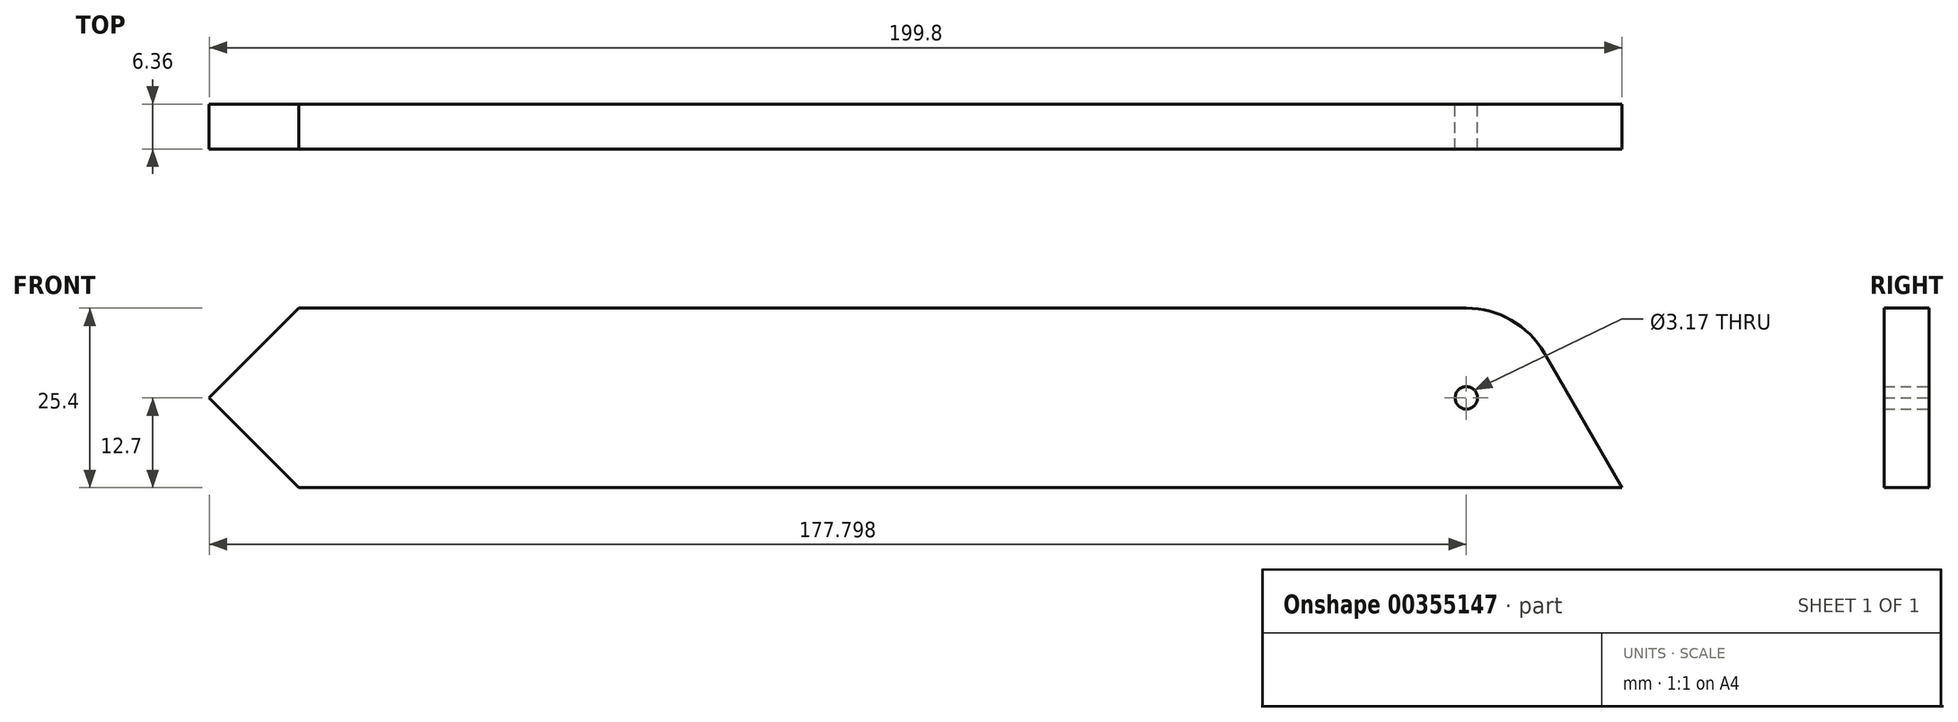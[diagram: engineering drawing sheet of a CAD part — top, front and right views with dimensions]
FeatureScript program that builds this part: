
annotation { "Feature Type Name" : "Feature", "Feature Type Description" : "" }
export const myFeature = defineFeature(function(context is Context, id is Id, definition is map)
    precondition{}
    {
        {
            var Q0;
            Q0=qCreatedBy(makeId("Front.planeOp"),FACE);
            var sketch = newSketch(context, id + "F0", { "sketchPlane" : qUnion([Q0])});
            skLineSegment(sketch, "E0", {"start": v(87.99, -152.4) * mm, "end": v(-263.96, -152.4) * mm});
            skLineSegment(sketch, "E1", {"start": v(-263.96, -152.4) * mm, "end": v(0, 0) * mm});
            skLineSegment(sketch, "E2", {"start": v(0, 0) * mm, "end": v(87.99, -152.4) * mm});
            skLineSegment(sketch, "E3", {"start": v(0, 0) * mm, "end": v(152.4, 87.99) * mm, "construction": true});
            skLineSegment(sketch, "E4", {"start": v(152.4, 87.99) * mm, "end": v(87.99, -152.4) * mm, "construction": true});
            skCircle(sketch, "E5", {"center": v(0, 0) * mm, "radius": 9.53 * mm});
            skCircle(sketch, "E6", {"center": v(0, 0) * mm, "radius": 12.7 * mm});
            skCircle(sketch, "E7", {"center": v(-263.96, -152.4) * mm, "radius": 12.7 * mm});
            skCircle(sketch, "E8", {"center": v(87.99, -152.4) * mm, "radius": 12.7 * mm});
            skLineSegment(sketch, "E9", {"start": v(-6.35, 11) * mm, "end": v(-270.31, -141.4) * mm});
            skLineSegment(sketch, "E10", {"start": v(-263.96, -165.1) * mm, "end": v(87.99, -165.1) * mm});
            skLineSegment(sketch, "E11", {"start": v(98.99, -146.05) * mm, "end": v(11, 6.35) * mm});
            skLineSegment(sketch, "E12", {"start": v(76.99, -158.75) * mm, "end": v(-11, -6.35) * mm});
            skLineSegment(sketch, "E13", {"start": v(-257.61, -163.4) * mm, "end": v(6.35, -11) * mm});
            skLineSegment(sketch, "E14", {"start": v(87.99, -139.7) * mm, "end": v(-263.96, -139.7) * mm});
            skLineSegment(sketch, "E15", {"start": v(87.99, -165.1) * mm, "end": v(109.99, -165.1) * mm});
            skLineSegment(sketch, "E16", {"start": v(98.99, -146.05) * mm, "end": v(109.99, -165.1) * mm});
            skCircle(sketch, "E17", {"center": v(87.99, -152.4) * mm, "radius": 1.59 * mm});
            skCircle(sketch, "E18", {"center": v(-263.96, -152.4) * mm, "radius": 1.59 * mm});
            skLineSegment(sketch, "E19", {"start": v(-270.31, -141.4) * mm, "end": v(-311.36, -165.1) * mm});
            skLineSegment(sketch, "E20", {"start": v(-263.96, -165.1) * mm, "end": v(-311.36, -165.1) * mm});
            skLineSegment(sketch, "E21", {"start": v(-77.11, -139.7) * mm, "end": v(-89.81, -152.4) * mm});
            skLineSegment(sketch, "E22", {"start": v(-89.81, -152.4) * mm, "end": v(-77.11, -165.1) * mm});
            skLineSegment(sketch, "E23", {"start": v(-77.11, -139.7) * mm, "end": v(-77.11, -165.1) * mm});
            skLineSegment(sketch, "E24", {"start": v(-158.96, -139.7) * mm, "end": v(-171.66, -152.4) * mm});
            skLineSegment(sketch, "E25", {"start": v(-171.66, -152.4) * mm, "end": v(-158.96, -165.1) * mm});
            skLineSegment(sketch, "E26", {"start": v(-158.96, -139.7) * mm, "end": v(-158.96, -165.1) * mm});
            skSolve(sketch);
        }
        {
            var Q0;
            {var subQ0=sQuery(id+"F0.wireOp",EDGE,"E12");var subQ1=sQuery(id+"F0.wireOp",EDGE,"E0");var subQ2=makeQuery(id+"F0.imprint","INTERSECT",VERTEX,{"derivedFrom":[subQ1,subQ0]});Q0=makeQuery(id+"F0.imprint","IMPRINT",FACE,{"disambiguationData":[TD([[makeQuery(id+"F0.imprint","IMPRINT",EDGE,{"disambiguationData":[TD([[subQ2,-1.0]])],"derivedFrom":subQ1}),-1.0]])]});}
            var Q1;
            {var subQ0=sQuery(id+"F0.wireOp",EDGE,"E22");Q1=makeQuery(id+"F0.imprint","IMPRINT",FACE,{"disambiguationData":[TD([[makeQuery(id+"F0.imprint","IMPRINT",EDGE,{"derivedFrom":subQ0}),1.0]])]});}
            var Q2;
            {var subQ0=sQuery(id+"F0.wireOp",EDGE,"E21");Q2=makeQuery(id+"F0.imprint","IMPRINT",FACE,{"disambiguationData":[TD([[makeQuery(id+"F0.imprint","IMPRINT",EDGE,{"derivedFrom":subQ0}),1.0]])]});}
            var Q3;
            {var subQ0=sQuery(id+"F0.wireOp",EDGE,"E12");var subQ3=sQuery(id+"F0.wireOp",EDGE,"E0");var subQ4=makeQuery(id+"F0.imprint","INTERSECT",VERTEX,{"derivedFrom":[subQ3,subQ0]});Q3=makeQuery(id+"F0.imprint","IMPRINT",FACE,{"disambiguationData":[TD([[makeQuery(id+"F0.imprint","IMPRINT",EDGE,{"disambiguationData":[TD([[subQ4,-1.0]])],"derivedFrom":subQ3}),1.0]])]});}
            var Q4;
            {var subQ3=sQuery(id+"F0.wireOp",EDGE,"E8");var subQ6=sQuery(id+"F0.wireOp",EDGE,"E0");var subQ9=makeQuery(id+"F0.imprint","INTERSECT",VERTEX,{"derivedFrom":[subQ6,subQ3]});Q4=makeQuery(id+"F0.imprint","IMPRINT",FACE,{"disambiguationData":[TD([[makeQuery(id+"F0.imprint","IMPRINT",EDGE,{"disambiguationData":[TD([[subQ9,-1.0]])],"derivedFrom":subQ6}),-1.0]])]});}
            var Q5;
            {var subQ0=sQuery(id+"F0.wireOp",EDGE,"E8");var subQ1=sQuery(id+"F0.wireOp",EDGE,"E0");var subQ2=makeQuery(id+"F0.imprint","INTERSECT",VERTEX,{"derivedFrom":[subQ1,subQ0]});Q5=makeQuery(id+"F0.imprint","IMPRINT",FACE,{"disambiguationData":[TD([[makeQuery(id+"F0.imprint","IMPRINT",EDGE,{"disambiguationData":[TD([[subQ2,-1.0]])],"derivedFrom":subQ1}),1.0]])]});}
            var Q6;
            {var subQ5=sQuery(id+"F0.wireOp",EDGE,"E17");var subQ7=sQuery(id+"F0.wireOp",EDGE,"E0");var subQ8=makeQuery(id+"F0.imprint","INTERSECT",VERTEX,{"derivedFrom":[subQ7,subQ5]});Q6=makeQuery(id+"F0.imprint","IMPRINT",FACE,{"disambiguationData":[TD([[makeQuery(id+"F0.imprint","IMPRINT",EDGE,{"disambiguationData":[TD([[subQ8,-1.0]])],"derivedFrom":subQ7}),1.0]])]});}
            var Q7;
            {var subQ0=sQuery(id+"F0.wireOp",EDGE,"E17");var subQ1=sQuery(id+"F0.wireOp",EDGE,"E0");var subQ2=makeQuery(id+"F0.imprint","INTERSECT",VERTEX,{"derivedFrom":[subQ1,subQ0]});Q7=makeQuery(id+"F0.imprint","IMPRINT",FACE,{"disambiguationData":[TD([[makeQuery(id+"F0.imprint","IMPRINT",EDGE,{"disambiguationData":[TD([[subQ2,-1.0]])],"derivedFrom":subQ1}),-1.0]])]});}
            var Q8;
            {var subQ0=sQuery(id+"F0.wireOp",EDGE,"E14");var subQ1=sQuery(id+"F0.wireOp",EDGE,"E2");var subQ2=makeQuery(id+"F0.imprint","INTERSECT",VERTEX,{"derivedFrom":[subQ1,subQ0]});Q8=makeQuery(id+"F0.imprint","IMPRINT",FACE,{"disambiguationData":[TD([[makeQuery(id+"F0.imprint","IMPRINT",EDGE,{"disambiguationData":[TD([[subQ2,-1.0]])],"derivedFrom":subQ1}),1.0]])]});}
            var Q9;
            {var subQ0=sQuery(id+"F0.wireOp",EDGE,"E15");Q9=makeQuery(id+"F0.imprint","IMPRINT",FACE,{"disambiguationData":[TD([[makeQuery(id+"F0.imprint","IMPRINT",EDGE,{"derivedFrom":subQ0}),1.0]])]});}
            extrude(context, id + "F1", {"entities" : qUnion([Q0, Q1, Q2, Q3, Q4, Q5, Q6, Q7, Q8, Q9]), "endBound" : BoundingType.SYMMETRIC, "depth" : 6.35 * mm});
        }
    });
